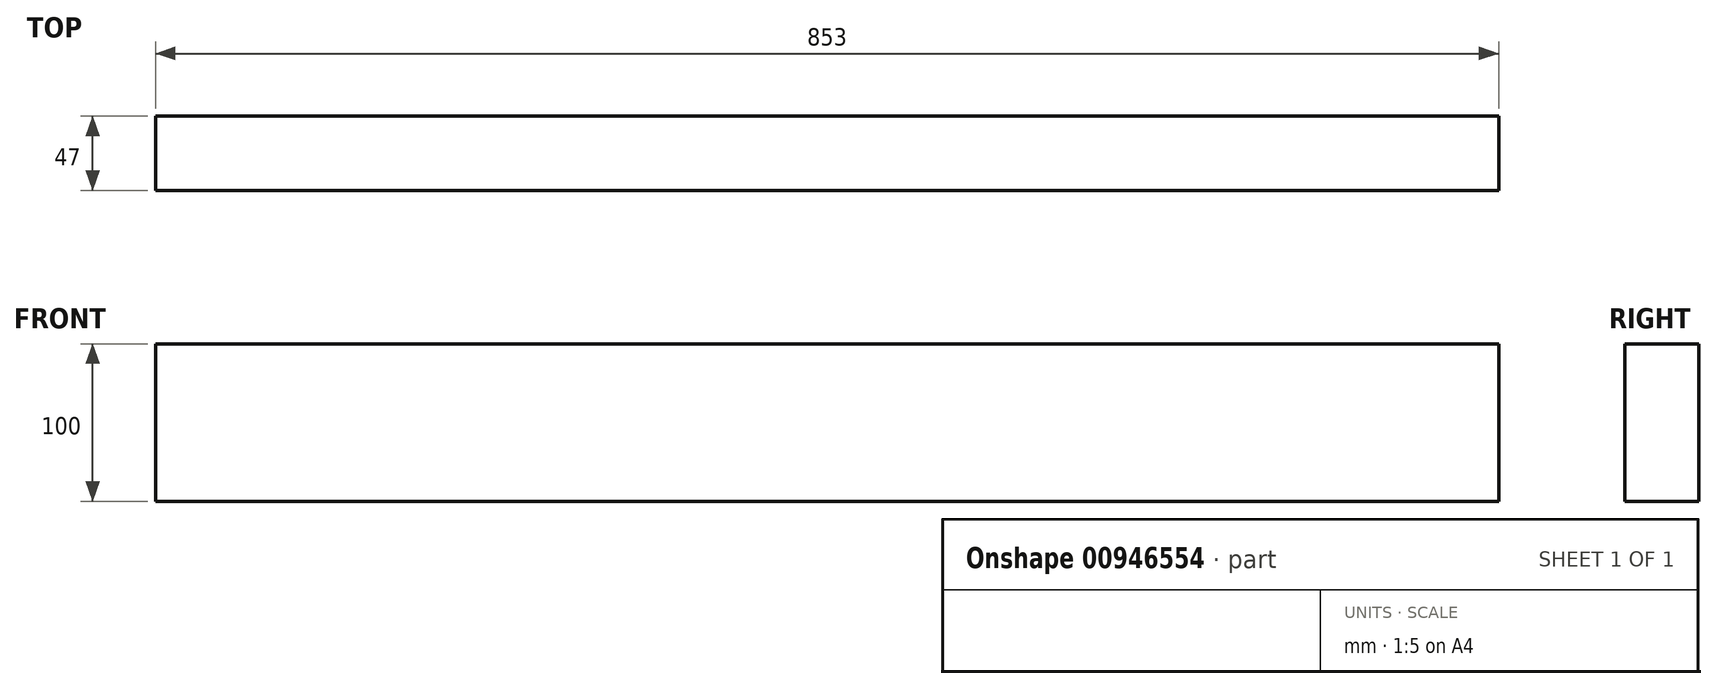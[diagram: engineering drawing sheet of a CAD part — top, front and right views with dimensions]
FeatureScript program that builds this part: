
annotation { "Feature Type Name" : "Feature", "Feature Type Description" : "" }
export const myFeature = defineFeature(function(context is Context, id is Id, definition is map)
    precondition{}
    {
        {
            var Q0;
            Q0=qCreatedBy(makeId("Right.planeOp"),FACE);
            var sketch = newSketch(context, id + "F0", { "sketchPlane" : qUnion([Q0])});
            skLineSegment(sketch, "E0.bottom", {"start": v(0, 0) * mm, "end": v(-47, 0) * mm});
            skLineSegment(sketch, "E0.top", {"start": v(0, 100) * mm, "end": v(-47, 100) * mm});
            skLineSegment(sketch, "E0.left", {"start": v(0, 0) * mm, "end": v(0, 100) * mm});
            skLineSegment(sketch, "E0.right", {"start": v(-47, 0) * mm, "end": v(-47, 100) * mm});
            skSolve(sketch);
        }
        {
            var Q0;
            Q0=qSketchRegion(id+"F0",true);
            extrude(context, id + "F1", {"entities" : qUnion([Q0]), "depth" : 853 * mm, "offsetDistance" : 25 * mm});
        }
    });
